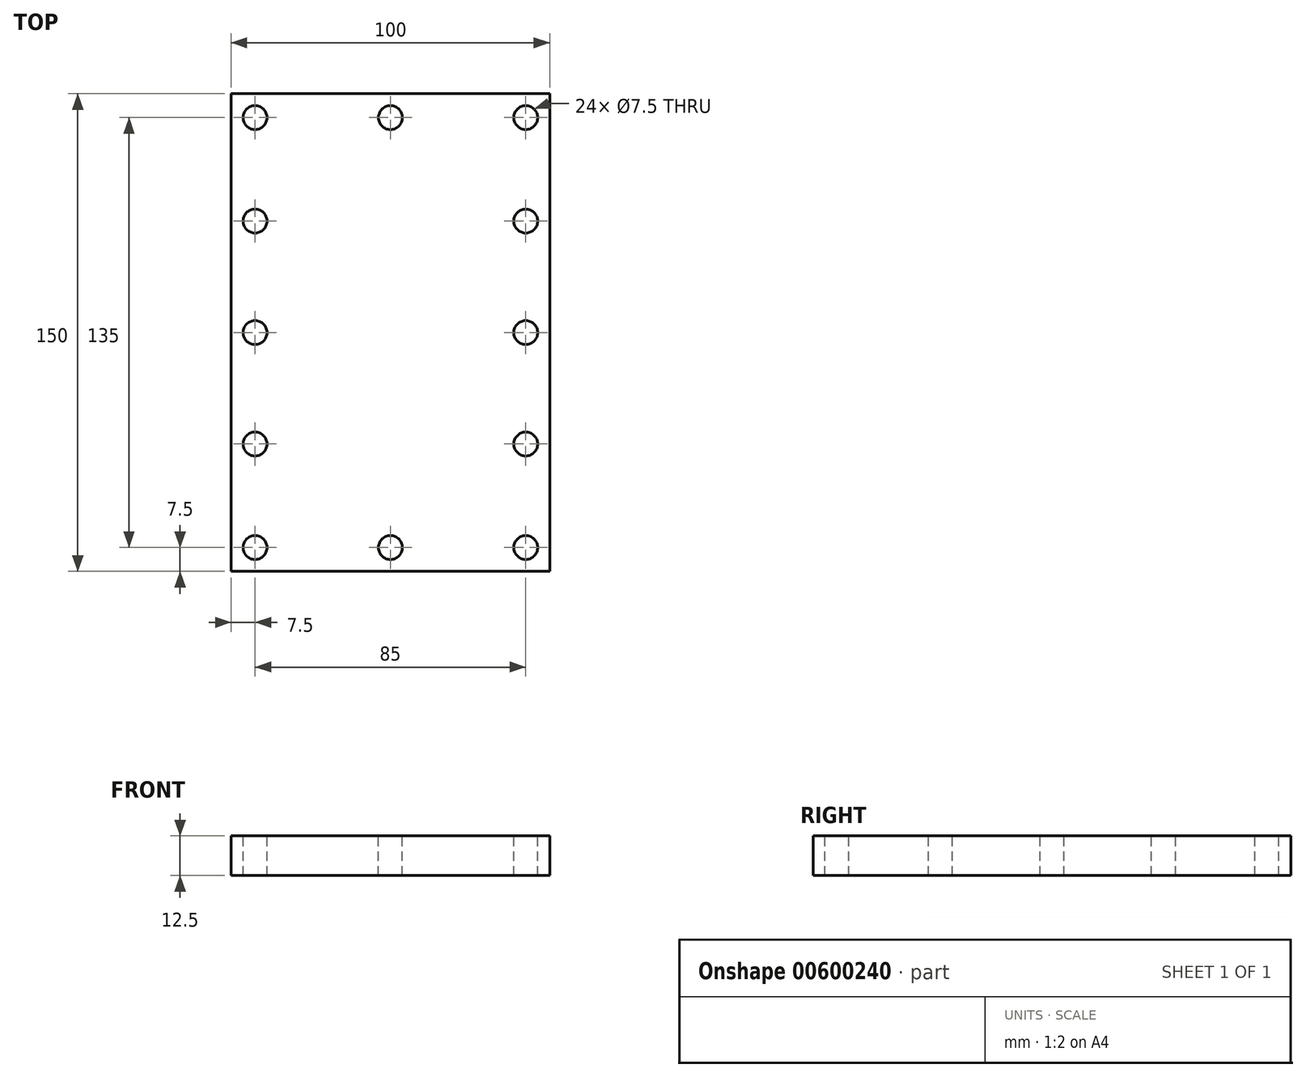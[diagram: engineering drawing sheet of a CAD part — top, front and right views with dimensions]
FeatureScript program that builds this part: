
annotation { "Feature Type Name" : "Feature", "Feature Type Description" : "" }
export const myFeature = defineFeature(function(context is Context, id is Id, definition is map)
    precondition{}
    {
        {
            var Q0;
            Q0=qCreatedBy(makeId("Top.planeOp"),FACE);
            var sketch = newSketch(context, id + "F0", { "sketchPlane" : qUnion([Q0])});
            skLineSegment(sketch, "E0.bottom", {"start": v(50, 75) * mm, "end": v(-50, 75) * mm});
            skLineSegment(sketch, "E0.top", {"start": v(50, -75) * mm, "end": v(-50, -75) * mm});
            skLineSegment(sketch, "E0.left", {"start": v(50, 75) * mm, "end": v(50, -75) * mm});
            skLineSegment(sketch, "E0.right", {"start": v(-50, 75) * mm, "end": v(-50, -75) * mm});
            skPoint(sketch, "E0.middle", {"position": v(0, 0) * mm});
            skSolve(sketch);
        }
        {
            var Q0;
            Q0 = qSketchRegion(id + "F0", true);
            var Q1;
            Q1 = qSketchRegion(id + "F2", true);
            extrude(context, id + "F1", {"entities" : qUnion([Q0, Q1]), "depth" : 12.5 * mm, "offsetDistance" : 25 * mm});
        }
        {
            var Q0;
            Q0=makeQuery(id+"F1.opExtrude","CAP_FACE",FACE,{"disambiguationData":[OSD([sQuery(id+"F0.wireOp",EDGE,"E0.bottom"),sQuery(id+"F0.wireOp",EDGE,"E0.top"),sQuery(id+"F0.wireOp",EDGE,"E0.left"),sQuery(id+"F0.wireOp",EDGE,"E0.right")])],"isStart":false});
            var sketch = newSketch(context, id + "F2", { "sketchPlane" : qUnion([Q0])});
            skCircle(sketch, "E1", {"center": v(-42.5, 67.5) * mm, "radius": 3.75 * mm});
            skCircle(sketch, "E2", {"center": v(-42.5, 0) * mm, "radius": 3.75 * mm});
            skCircle(sketch, "E3", {"center": v(-42.5, -35) * mm, "radius": 3.75 * mm});
            skCircle(sketch, "E4", {"center": v(-42.5, -67.5) * mm, "radius": 3.75 * mm});
            skCircle(sketch, "E5", {"center": v(0, -67.5) * mm, "radius": 3.75 * mm});
            skCircle(sketch, "E6", {"center": v(-42.5, 35) * mm, "radius": 3.75 * mm});
            skCircle(sketch, "E7", {"center": v(42.5, -67.5) * mm, "radius": 3.75 * mm});
            skCircle(sketch, "E8", {"center": v(42.5, -35) * mm, "radius": 3.75 * mm});
            skCircle(sketch, "E9", {"center": v(42.5, 0) * mm, "radius": 3.75 * mm});
            skCircle(sketch, "E10", {"center": v(42.5, 35) * mm, "radius": 3.75 * mm});
            skCircle(sketch, "E11", {"center": v(42.5, 67.5) * mm, "radius": 3.75 * mm});
            skCircle(sketch, "E12", {"center": v(0, 67.5) * mm, "radius": 3.75 * mm});
            skSolve(sketch);
        }
        {
            var Q0;
            Q0 = qSketchRegion(id + "F2", true);
            extrude(context, id + "F3", {"entities" : qUnion([Q0]), "operationType" : NewBodyOperationType.REMOVE, "oppositeDirection" : true, "depth" : 25 * mm, "offsetDistance" : 25 * mm});
        }
    });
